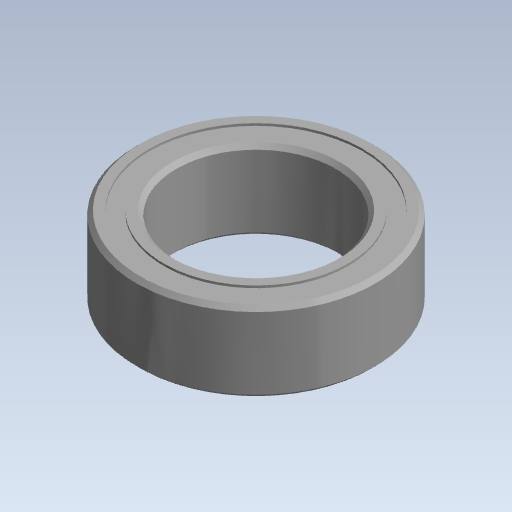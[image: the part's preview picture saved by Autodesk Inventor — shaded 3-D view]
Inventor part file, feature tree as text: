
AUTODESK INVENTOR PART (.ipt)
format: ipt  version: 2020 (Build 240168000, 168)  size: 551,936 bytes
history: native  units: mm (DEFAULTED — no unit token found)
features: other x11, revolve x5
ambient origin geometry x8: Origin, YZ Plane, XZ Plane, XY Plane, X Axis, Y Axis, Z Axis, Center Point
bodies: Solid1 (feature_tree), Solid2 (feature_tree), Solid3 (feature_tree), Solid4 (feature_tree), Solid5 (feature_tree), Solid6 (feature_tree), Solid7 (feature_tree), Solid8 (feature_tree), Solid9 (feature_tree), Solid10 (feature_tree), Solid11 (feature_tree), Solid12 (feature_tree), Solid13 (feature_tree), Solid14 (feature_tree), Solid15 (feature_tree), Solid16 (feature_tree)
feature tree (16):
  revolve  "Revolve1"  [1 undecoded]
  revolve  "Revolve3"  [1 undecoded]
  revolve  "Revolve4"  [1 undecoded]
  other  "CirPattern1[1]"
  other  "CirPattern1[2]"
  other  "CirPattern1[3]"
  other  "CirPattern1[4]"
  other  "CirPattern1[5]"
  other  "CirPattern1[6]"
  other  "CirPattern1[7]"
  other  "CirPattern1[8]"
  other  "CirPattern1[9]"
  other  "CirPattern1[10]"
  other  "CirPattern1[11]"
  revolve  "Revolve5[1]"  [1 undecoded]
  revolve  "Revolve5[2]"  [1 undecoded]
note: 5 required parameter values undecoded (feature->parameter linkage not recoverable at this tier; creation-order binding heuristic only, values carry confidence <= 0.55)
